AUTODESK INVENTOR PART (.ipt)
format: ipt  version: 2015 (Build 190159000, 159)  size: 185,344 bytes
history: native  units: in
note: dims shown in document units (in); Inventor stores cm internally (conversion verified against a paired STEP export)
features: reference x14, sketch x11, extrude x8, projected_geometry x3, plane x2, move_body x2, direct_edit x1, other x1
ambient origin geometry x8: Origin, YZ Plane, XZ Plane, XY Plane, X Axis, Y Axis, Z Axis, Center Point
bodies: Solid1 (feature_tree)
feature tree (42):
  plane  "Work Plane1"
  plane  "Work Plane2"
  extrude  "Extrusion1"  Depth=2.4375in TaperAngle=0.0deg
  extrude  "Extrusion2"  Depth=0.75in TaperAngle=0.0deg
  extrude  "Extrusion3"  TaperAngle=180.0deg  [1 undecoded]
  extrude  "Extrusion4"  Depth=0.5in
  extrude  "Extrusion5"  Depth=0.5in TaperAngle=0.0deg
  extrude  "Extrusion6"  TaperAngle=0.0deg  [1 undecoded]
  sketch  "Sketch10"  dims[d26=0.0in d27=0.0in d29=0.1406in]
  extrude  "Extrusion7"  Depth=0.1406in
  sketch  "Sketch12"  dims[d32=0.1406in]
  direct_edit  "Direct Edit1"
  extrude  "Extrusion8"  Depth=0.1406in
  sketch  "Sketch14"
  sketch  "Sketch2"  dims[d0=2.4375in d1=0.0in d2=2.4375in d3=0.0in]
  reference  "Reference1"
  reference  "Reference2"
  sketch  "Sketch3"  dims[d4=2.4375in d5=0.0in d6=0.75in d7=0.0in]
  reference  "Reference3"
  reference  "Reference4"
  reference  "Reference5"
  reference  "Reference6"
  sketch  "Sketch4"  dims[d8=0.5625in d9=0.0in d10=180.0deg]
  reference  "Reference7"
  reference  "Reference8"
  reference  "Reference9"
  reference  "Reference10"
  sketch  "Sketch6"  dims[d11=0.5in d12=0.0in d13=0.1406in]
  projected_geometry  "Projected Loop1"
  sketch  "Sketch7"  dims[d14=0.1406in d15=0.5in d16=0.0in]
  reference  "Reference13"
  reference  "Reference14"
  reference  "Reference15"
  reference  "Reference16"
  sketch  "Sketch8"  dims[d20=0.0in d21=0.0in d22=1.25in d23=0.0in d24=0.0in d25=-2.309in]
  projected_geometry  "Projected Loop2"
  sketch  "Sketch11"  dims[d30=0.1406in d31=0.1406in]
  projected_geometry  "Projected Loop3"
  sketch  "Sketch13"
  move_body  "Move1"
  other  "Delete1"
  move_body  "Move2"
note: 2 required parameter values undecoded (feature->parameter linkage not recoverable at this tier; creation-order binding heuristic only, values carry confidence <= 0.55)
